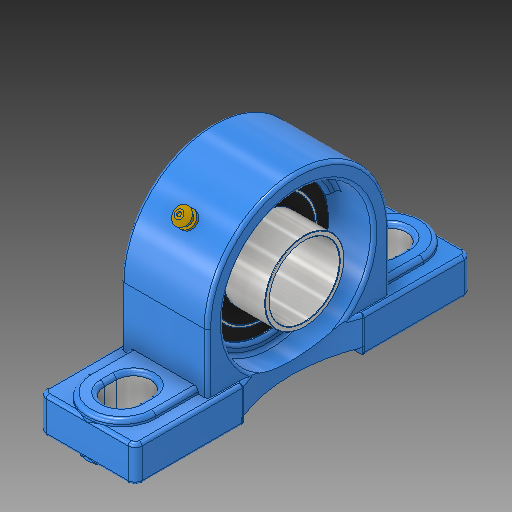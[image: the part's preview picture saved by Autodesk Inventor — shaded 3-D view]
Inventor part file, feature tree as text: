
AUTODESK INVENTOR PART (.ipt)
format: ipt  version: 2019 (Build 230136000, 136)  size: 674,304 bytes
history: native  units: in
note: dims shown in document units (in); Inventor stores cm internally (conversion verified against a paired STEP export)
features: sketch x28, plane x7, other x3
ambient origin geometry x8: Origin, YZ Plane, XZ Plane, XY Plane, X Axis, Y Axis, Z Axis, Center Point
bodies: Solid1 (feature_tree)
feature tree (38):
  other  "Pillow Bearing inventor.ipt"
  other  "Solid1::Pillow Bearing inventor.ipt"
  other  "TaggingFeature1"
  sketch  "Sketch1"  dims[d0=0.3937in]
  sketch  "Sketch2"
  sketch  "Sketch3"
  sketch  "Sketch4"
  sketch  "Sketch5"
  sketch  "Sketch6"
  sketch  "Sketch7"
  sketch  "Sketch8"
  sketch  "Sketch9"
  sketch  "Sketch10"
  sketch  "Sketch11"
  sketch  "Sketch13"
  sketch  "Sketch14"
  sketch  "Sketch15"
  sketch  "Sketch17"
  sketch  "Sketch18"
  sketch  "Sketch19"
  sketch  "Sketch20"
  sketch  "Sketch21"
  sketch  "Sketch22"
  sketch  "Sketch23"
  sketch  "Sketch24"
  sketch  "Sketch25"
  sketch  "Sketch26"
  sketch  "Sketch27"
  sketch  "Sketch28"
  sketch  "Sketch29"
  sketch  "Sketch30"
  plane  "Work Plane1"
  plane  "Work Plane2"
  plane  "Work Plane5"
  plane  "Work Plane6"
  plane  "Work Plane7"
  plane  "Work Plane8"
  plane  "Work Plane9"
